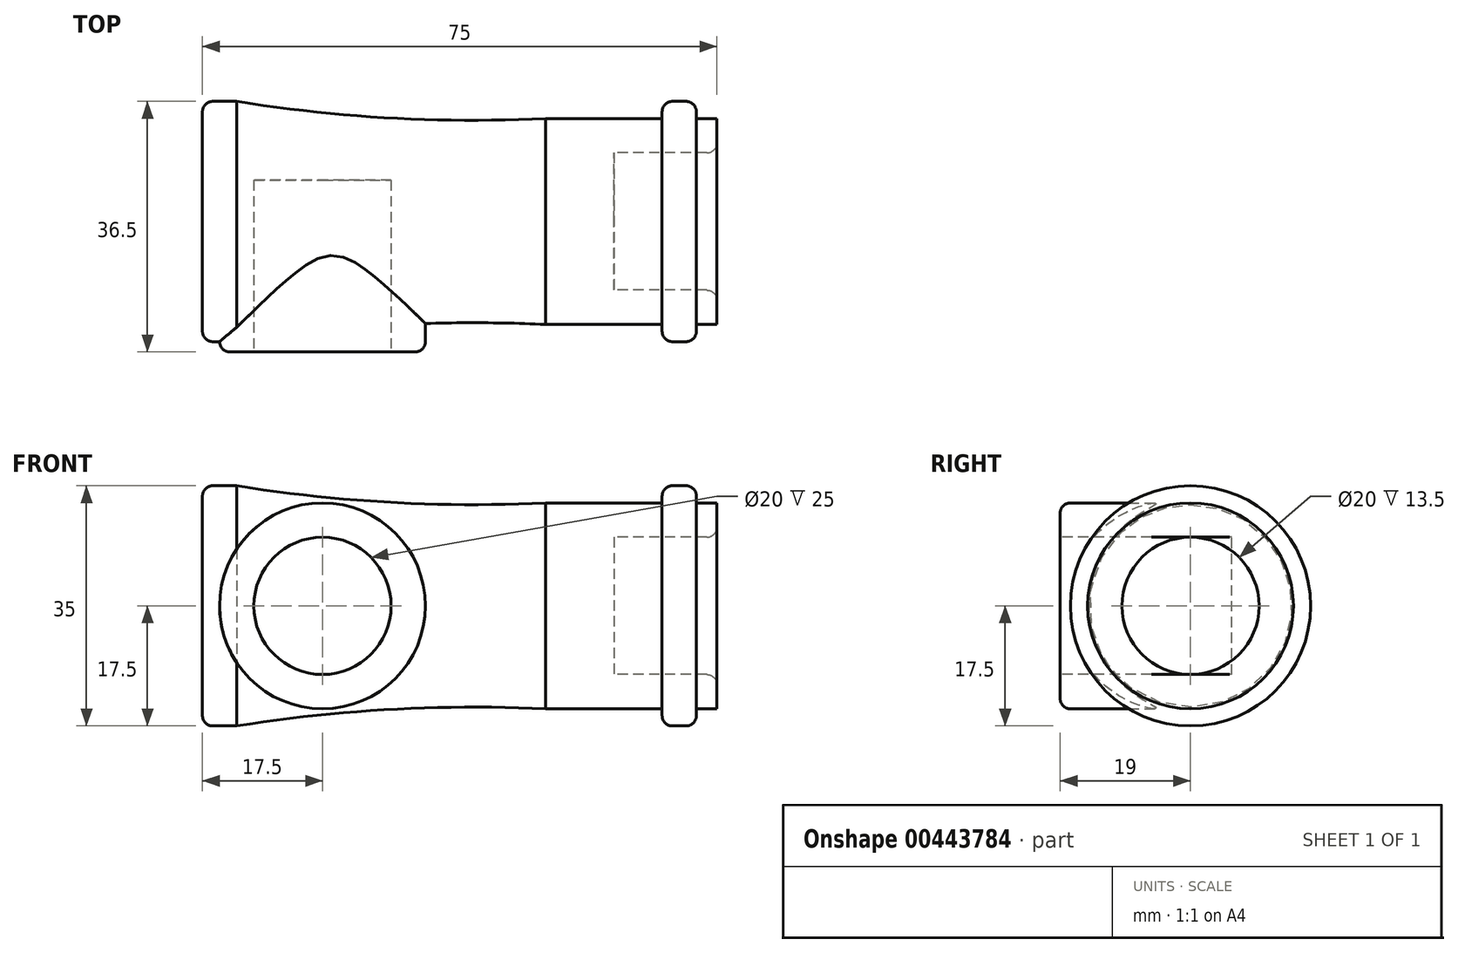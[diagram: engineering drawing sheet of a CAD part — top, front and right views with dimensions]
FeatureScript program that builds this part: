
annotation { "Feature Type Name" : "Feature", "Feature Type Description" : "" }
export const myFeature = defineFeature(function(context is Context, id is Id, definition is map)
    precondition{}
    {
        {
            var Q0;
            Q0=qCreatedBy(makeId("Front.planeOp"),FACE);
            var sketch = newSketch(context, id + "F0", { "sketchPlane" : qUnion([Q0])});
            skLineSegment(sketch, "E0", {"start": v(0, 17.5) * mm, "end": v(0, 0) * mm});
            skLineSegment(sketch, "E1", {"start": v(0, 0) * mm, "end": v(60, 0) * mm});
            skLineSegment(sketch, "E2", {"start": v(60, 0) * mm, "end": v(60, 10) * mm});
            skLineSegment(sketch, "E3", {"start": v(60, 10) * mm, "end": v(75, 10) * mm});
            skLineSegment(sketch, "E4", {"start": v(75, 10) * mm, "end": v(75, 15) * mm});
            skLineSegment(sketch, "E5", {"start": v(75, 15) * mm, "end": v(72, 15) * mm});
            skLineSegment(sketch, "E6", {"start": v(72, 15) * mm, "end": v(72, 17.5) * mm});
            skLineSegment(sketch, "E7", {"start": v(72, 17.5) * mm, "end": v(67, 17.5) * mm});
            skLineSegment(sketch, "E8", {"start": v(67, 17.5) * mm, "end": v(67, 15) * mm});
            skLineSegment(sketch, "E9", {"start": v(67, 15) * mm, "end": v(50, 15) * mm});
            skLineSegment(sketch, "E10", {"start": v(5, 17.5) * mm, "end": v(0, 17.5) * mm});
            skArc(sketch, "E11", {"start": v(5, 17.5) * mm, "mid": v(27.44, 15.08) * mm, "end": v(50, 15) * mm});
            skSolve(sketch);
        }
        {
            var Q0;
            Q0 = qSketchRegion(id + "F0", true);
            var Q1;
            Q1=sQuery(id+"F0.wireOp",EDGE,"E1");
            revolve(context, id + "F1", {"entities" : qUnion([Q0]), "axis" : qUnion([Q1]), "revolveType" : RevolveType.FULL});
        }
        {
            var Q0;
            Q0=qCreatedBy(makeId("Front.planeOp"),FACE);
            var sketch = newSketch(context, id + "F2", { "sketchPlane" : qUnion([Q0])});
            skCircle(sketch, "E12", {"center": v(17.5, 0) * mm, "radius": 15 * mm});
            skSolve(sketch);
        }
        {
            var Q0;
            Q0 = qSketchRegion(id + "F2", true);
            extrude(context, id + "F3", {"entities" : qUnion([Q0]), "operationType" : NewBodyOperationType.ADD, "depth" : 19 * mm});
        }
        {
            var Q0;
            Q0=makeQuery(id+"F3.opExtrude","CAP_FACE",FACE,{"disambiguationData":[OSD([sQuery(id+"F2.wireOp",EDGE,"E12")])],"isStart":false});
            var sketch = newSketch(context, id + "F4", { "sketchPlane" : qUnion([Q0])});
            skCircle(sketch, "E13", {"center": v(17.5, 0) * mm, "radius": 10 * mm});
            skSolve(sketch);
        }
        {
            var Q0;
            Q0 = qSketchRegion(id + "F4", true);
            extrude(context, id + "F5", {"entities" : qUnion([Q0]), "operationType" : NewBodyOperationType.REMOVE, "oppositeDirection" : true, "depth" : 25 * mm});
        }
        {
            var Q0;
            Q0=makeQuery(id+"F1.opRevolve","SWEPT_EDGE",EDGE,{"disambiguationData":[OSD([sQuery(id+"F0.wireOp",EDGE,"E0"),sQuery(id+"F0.wireOp",EDGE,"E10")])]});
            var Q1;
            Q1=makeQuery(id+"F3.opExtrude","CAP_EDGE",EDGE,{"disambiguationData":[OSD([sQuery(id+"F2.wireOp",EDGE,"E12")])],"isStart":false});
            var Q2;
            Q2=makeQuery(id+"F1.opRevolve","SWEPT_EDGE",EDGE,{"disambiguationData":[OSD([sQuery(id+"F0.wireOp",EDGE,"E7"),sQuery(id+"F0.wireOp",EDGE,"E8")])]});
            var Q3;
            Q3=makeQuery(id+"F1.opRevolve","SWEPT_EDGE",EDGE,{"disambiguationData":[OSD([sQuery(id+"F0.wireOp",EDGE,"E3"),sQuery(id+"F0.wireOp",EDGE,"E4")])]});
            fillet(context, id + "F6", {"entities" : qUnion([Q0, Q1, Q2, Q3]), "radius" : 1.5 * mm, "tangentPropagation" : true, "allowEdgeOverflow" : false});
        }
        {
            var Q0;
            Q0=makeQuery(id+"F1.opRevolve","SWEPT_EDGE",EDGE,{"disambiguationData":[OSD([sQuery(id+"F0.wireOp",EDGE,"E6"),sQuery(id+"F0.wireOp",EDGE,"E7")])]});
            fillet(context, id + "F7", {"entities" : qUnion([Q0]), "radius" : 1.5 * mm, "tangentPropagation" : true, "allowEdgeOverflow" : false});
        }
    });
